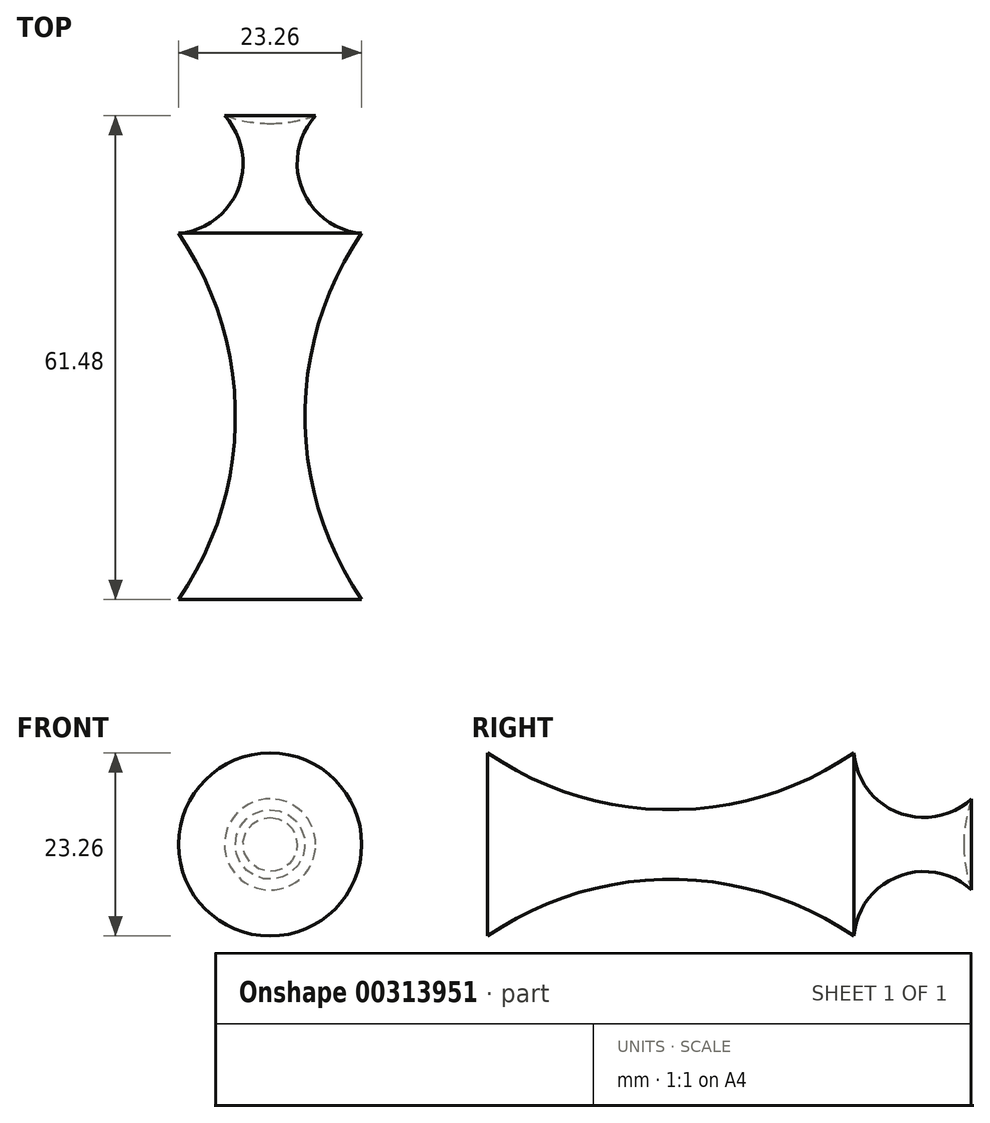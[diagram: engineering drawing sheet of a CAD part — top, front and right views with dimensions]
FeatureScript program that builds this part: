
annotation { "Feature Type Name" : "Feature", "Feature Type Description" : "" }
export const myFeature = defineFeature(function(context is Context, id is Id, definition is map)
    precondition{}
    {
        {
            var Q0;
            Q0=qCreatedBy(makeId("Top.planeOp"),FACE);
            var sketch = newSketch(context, id + "F0", { "sketchPlane" : qUnion([Q0])});
            skLineSegment(sketch, "E0", {"start": v(0, 52.56) * mm, "end": v(0, 0) * mm});
            skArc(sketch, "E1", {"start": v(0, 18.14) * mm, "mid": v(17.21, 35.35) * mm, "end": v(0, 52.56) * mm});
            skArc(sketch, "E2", {"start": v(5.8, 19.15) * mm, "mid": v(4.05, 9.85) * mm, "end": v(11.63, 4.19) * mm});
            skArc(sketch, "E3", {"start": v(11.63, 4.19) * mm, "mid": v(4.42, -19.07) * mm, "end": v(11.63, -42.33) * mm});
            skLineSegment(sketch, "E4", {"start": v(11.63, -42.33) * mm, "end": v(0, -42.33) * mm});
            skLineSegment(sketch, "E5", {"start": v(0, 52.56) * mm, "end": v(0, -42.33) * mm});
            skSolve(sketch);
        }
        {
            var Q0;
            {var subQ0=sQuery(id+"F0.wireOp",EDGE,"E5");var subQ1=sQuery(id+"F0.wireOp",EDGE,"E1");var subQ2=makeQuery(id+"F0.imprint","INTERSECT",VERTEX,{"disambiguationData":[OD(0.0)],"derivedFrom":[subQ1,subQ0]});Q0=makeQuery(id+"F0.imprint","IMPRINT",FACE,{"disambiguationData":[TD([[makeQuery(id+"F0.imprint","IMPRINT",EDGE,{"disambiguationData":[TD([[subQ2,-1.0]])],"derivedFrom":subQ1}),1.0]])]});}
            var Q1;
            {var subQ1=sQuery(id+"F0.wireOp",EDGE,"E2");Q1=makeQuery(id+"F0.imprint","IMPRINT",FACE,{"disambiguationData":[TD([[makeQuery(id+"F0.imprint","IMPRINT",EDGE,{"derivedFrom":subQ1}),-1.0]])]});}
            var Q2;
            Q2=sQuery(id+"F0.wireOp",EDGE,"E5");
            revolve(context, id + "F1", {"entities" : qUnion([Q0, Q1]), "axis" : qUnion([Q2]), "revolveType" : RevolveType.FULL});
        }
    });
